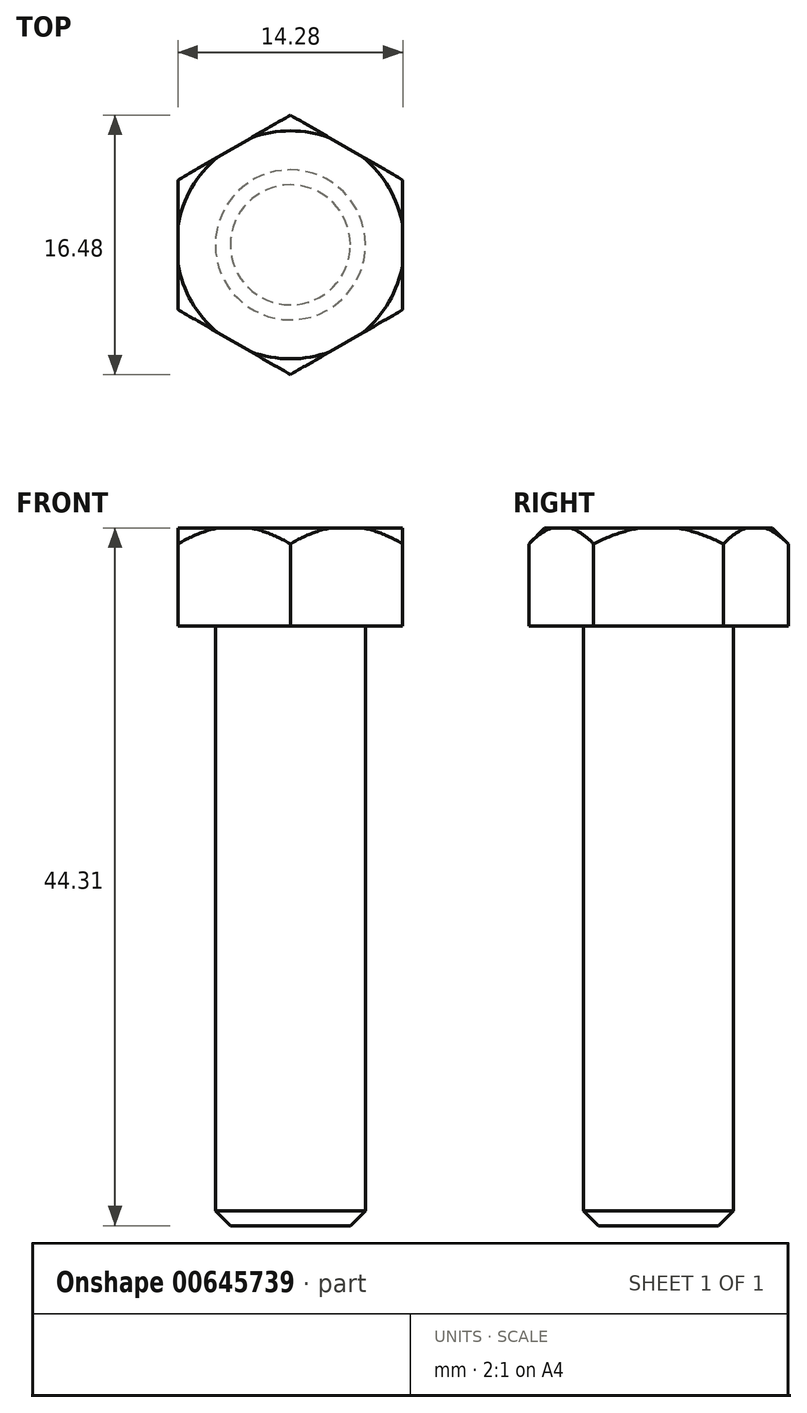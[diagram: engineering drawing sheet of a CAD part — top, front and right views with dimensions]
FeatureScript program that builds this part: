
annotation { "Feature Type Name" : "Feature", "Feature Type Description" : "" }
export const myFeature = defineFeature(function(context is Context, id is Id, definition is map)
    precondition{}
    {
        {
            var Q0;
            Q0=qCreatedBy(makeId("Top.planeOp"),FACE);
            var sketch = newSketch(context, id + "F0", { "sketchPlane" : qUnion([Q0])});
            skCircle(sketch, "E0.cCircle", {"center": v(0, 0) * mm, "radius": 7.13 * mm, "construction": true});
            skLineSegment(sketch, "E0.0", {"start": v(0, 8.24) * mm, "end": v(7.13, 4.12) * mm});
            skLineSegment(sketch, "E0.1", {"start": v(7.13, 4.12) * mm, "end": v(7.14, -4.12) * mm});
            skLineSegment(sketch, "E0.2", {"start": v(7.13, -4.12) * mm, "end": v(0, -8.24) * mm});
            skLineSegment(sketch, "E0.3", {"start": v(0, -8.24) * mm, "end": v(-7.14, -4.12) * mm});
            skLineSegment(sketch, "E0.4", {"start": v(-7.13, -4.12) * mm, "end": v(-7.14, 4.12) * mm});
            skLineSegment(sketch, "E0.5", {"start": v(-7.13, 4.12) * mm, "end": v(0, 8.24) * mm});
            skPoint(sketch, "E0.0.midPoint", {"position": v(3.57, 6.18) * mm});
            skSolve(sketch);
        }
        {
            var Q0;
            Q0=makeQuery(id+"F0.imprint","IMPRINT",FACE,{"disambiguationData":[TD([[makeQuery(id+"F0.imprint","IMPRINT",EDGE,{"derivedFrom":sQuery(id+"F0.wireOp",EDGE,"E0.0")}),-1.0]])]});
            extrude(context, id + "F1", {"entities" : qUnion([Q0]), "oppositeDirection" : true, "depth" : 6.2 * mm, "offsetDistance" : 25 * mm});
        }
        {
            var Q0;
            Q0=makeQuery(id+"F1.opExtrude","CAP_FACE",FACE,{"disambiguationData":[OSD([sQuery(id+"F0.wireOp",EDGE,"E0.0"),sQuery(id+"F0.wireOp",EDGE,"E0.1"),sQuery(id+"F0.wireOp",EDGE,"E0.2"),sQuery(id+"F0.wireOp",EDGE,"E0.3"),sQuery(id+"F0.wireOp",EDGE,"E0.4"),sQuery(id+"F0.wireOp",EDGE,"E0.5")])],"isStart":false});
            var sketch = newSketch(context, id + "F2", { "sketchPlane" : qUnion([Q0])});
            skCircle(sketch, "E1", {"center": v(0, 0) * mm, "radius": 4.76 * mm});
            skSolve(sketch);
        }
        {
            var Q0;
            Q0=makeQuery(id+"F2.imprint","IMPRINT",FACE,{"disambiguationData":[TD([[makeQuery(id+"F2.imprint","IMPRINT",EDGE,{"derivedFrom":sQuery(id+"F2.wireOp",EDGE,"E1")}),1.0]])]});
            extrude(context, id + "F3", {"entities" : qUnion([Q0]), "operationType" : NewBodyOperationType.ADD, "depth" : 38.1 * mm, "offsetDistance" : 25 * mm});
        }
        {
            var Q0;
            Q0=makeQuery(id+"F3.opExtrude","CAP_EDGE",EDGE,{"disambiguationData":[OSD([sQuery(id+"F2.wireOp",EDGE,"E1")])],"isStart":false});
            chamfer(context, id + "F4", {"entities" : qUnion([Q0]), "chamferType" : ChamferType.OFFSET_ANGLE, "width" : .95 * mm, "oppositeDirection" : false, "angle" : 45 * degree, "tangentPropagation" : true});
        }
        {
            var Q0;
            Q0=qCreatedBy(makeId("Right.planeOp"),FACE);
            var sketch = newSketch(context, id + "F5", { "sketchPlane" : qUnion([Q0])});
            skLineSegment(sketch, "E2", {"start": v(7.24, 0) * mm, "end": v(8.24, -1) * mm});
            skLineSegment(sketch, "E3", {"start": v(8.24, -1) * mm, "end": v(8.24, 0) * mm});
            skLineSegment(sketch, "E4", {"start": v(8.24, 0) * mm, "end": v(7.24, 0) * mm});
            skSolve(sketch);
        }
        {
            var Q0;
            Q0 = qSketchRegion(id + "F5", true);
            var Q1;
            Q1=makeQuery(id+"F3.opExtrude","SWEPT_FACE",FACE,{"disambiguationData":[OSD([sQuery(id+"F2.wireOp",EDGE,"E1")])]});
            revolve(context, id + "F6", {"operationType" : NewBodyOperationType.REMOVE, "entities" : qUnion([Q0]), "axis" : qUnion([Q1]), "revolveType" : RevolveType.FULL, "oppositeDirection" : true});
        }
    });
